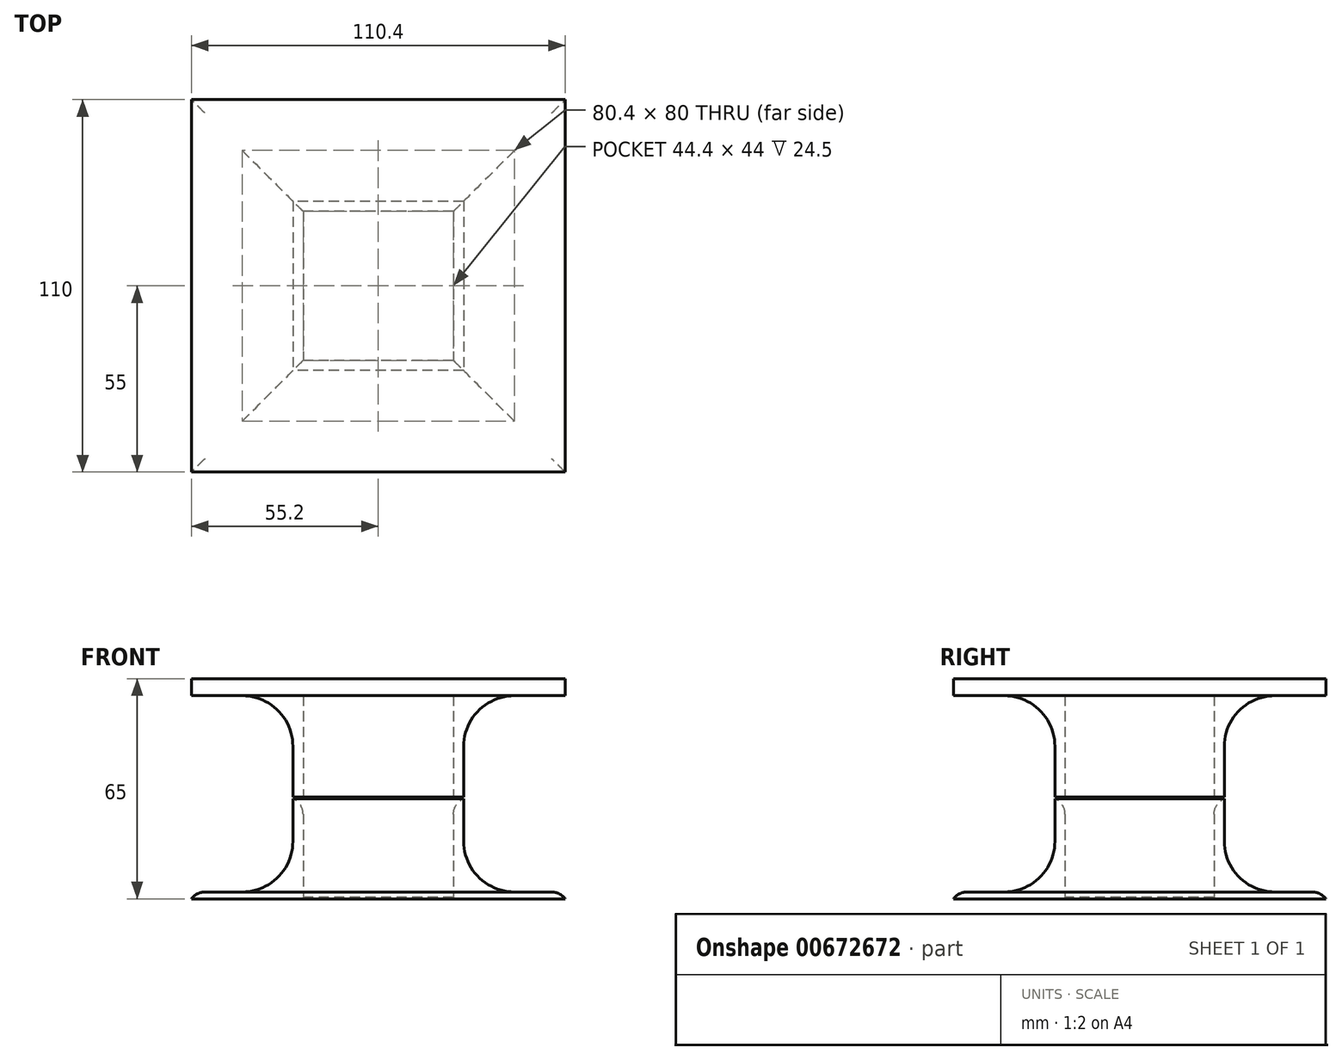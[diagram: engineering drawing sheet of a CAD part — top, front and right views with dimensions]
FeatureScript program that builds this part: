
annotation { "Feature Type Name" : "Feature", "Feature Type Description" : "" }
export const myFeature = defineFeature(function(context is Context, id is Id, definition is map)
    precondition{}
    {
        {
            var Q0;
            Q0=qCreatedBy(makeId("Top.planeOp"),FACE);
            var sketch = newSketch(context, id + "F0", { "sketchPlane" : qUnion([Q0])});
            skLineSegment(sketch, "E0.bottom", {"start": v(22.2, 22) * mm, "end": v(-22.2, 22) * mm});
            skLineSegment(sketch, "E0.top", {"start": v(22.2, -22) * mm, "end": v(-22.2, -22) * mm});
            skLineSegment(sketch, "E0.left", {"start": v(22.2, 22) * mm, "end": v(22.2, -22) * mm});
            skLineSegment(sketch, "E0.right", {"start": v(-22.2, 22) * mm, "end": v(-22.2, -22) * mm});
            skPoint(sketch, "E0.middle", {"position": v(0, 0) * mm});
            skLineSegment(sketch, "E1.bottom", {"start": v(55.2, 55) * mm, "end": v(-55.2, 55) * mm});
            skLineSegment(sketch, "E1.top", {"start": v(55.2, -55) * mm, "end": v(-55.2, -55) * mm});
            skLineSegment(sketch, "E1.left", {"start": v(55.2, 55) * mm, "end": v(55.2, -55) * mm});
            skLineSegment(sketch, "E1.right", {"start": v(-55.2, 55) * mm, "end": v(-55.2, -55) * mm});
            skLineSegment(sketch, "E2.0", {"start": v(25.2, 25) * mm, "end": v(25.2, -25) * mm});
            skLineSegment(sketch, "E2.1", {"start": v(25.2, 25) * mm, "end": v(-25.2, 25) * mm});
            skLineSegment(sketch, "E2.2", {"start": v(-25.2, 25) * mm, "end": v(-25.2, -25) * mm});
            skLineSegment(sketch, "E2.3", {"start": v(25.2, -25) * mm, "end": v(-25.2, -25) * mm});
            skLineSegment(sketch, "E3", {"start": v(25.2, 25) * mm, "end": v(25.2, 55) * mm, "construction": true});
            skLineSegment(sketch, "E4", {"start": v(25.2, 25) * mm, "end": v(55.2, 25) * mm, "construction": true});
            skSolve(sketch);
        }
        {
            var Q0;
            Q0=makeQuery(id+"F0.imprint","IMPRINT",FACE,{"disambiguationData":[TD([[makeQuery(id+"F0.imprint","IMPRINT",EDGE,{"derivedFrom":sQuery(id+"F0.wireOp",EDGE,"E1.bottom")}),1.0]])]});
            var Q1;
            Q1=makeQuery(id+"F0.imprint","IMPRINT",FACE,{"disambiguationData":[TD([[makeQuery(id+"F0.imprint","IMPRINT",EDGE,{"derivedFrom":sQuery(id+"F0.wireOp",EDGE,"E0.bottom")}),-1.0]])]});
            extrude(context, id + "F1", {"entities" : qUnion([Q0, Q1]), "depth" : 2 * mm, "offsetDistance" : 25 * mm});
        }
        {
            var Q0;
            Q0=makeQuery(id+"F0.imprint","IMPRINT",FACE,{"disambiguationData":[TD([[makeQuery(id+"F0.imprint","IMPRINT",EDGE,{"derivedFrom":sQuery(id+"F0.wireOp",EDGE,"E0.bottom")}),-1.0]])]});
            extrude(context, id + "F2", {"entities" : qUnion([Q0]), "operationType" : NewBodyOperationType.ADD, "depth" : 30 * mm, "offsetDistance" : 25 * mm});
        }
        {
            var Q0;
            Q0=makeQuery(id+"F2.opExtrude","CAP_FACE",FACE,{"disambiguationData":[OSD([sQuery(id+"F0.wireOp",EDGE,"E0.bottom"),sQuery(id+"F0.wireOp",EDGE,"E0.top"),sQuery(id+"F0.wireOp",EDGE,"E0.left"),sQuery(id+"F0.wireOp",EDGE,"E0.right"),sQuery(id+"F0.wireOp",EDGE,"E2.0"),sQuery(id+"F0.wireOp",EDGE,"E2.1"),sQuery(id+"F0.wireOp",EDGE,"E2.2"),sQuery(id+"F0.wireOp",EDGE,"E2.3")])],"isStart":false});
            extrude(context, id + "F3", {"entities" : qUnion([Q0]), "depth" : 30 * mm, "offsetDistance" : 25 * mm});
        }
        {
            var Q0;
            Q0=makeQuery(id+"F0.imprint","IMPRINT",FACE,{"disambiguationData":[TD([[makeQuery(id+"F0.imprint","IMPRINT",EDGE,{"derivedFrom":sQuery(id+"F0.wireOp",EDGE,"E0.bottom")}),1.0]])]});
            extrude(context, id + "F4", {"entities" : qUnion([Q0]), "operationType" : NewBodyOperationType.ADD, "depth" : 0.5 * mm, "offsetDistance" : 25 * mm});
        }
        {
            var Q0;
            Q0=makeQuery(id+"F0.imprint","IMPRINT",FACE,{"disambiguationData":[TD([[makeQuery(id+"F0.imprint","IMPRINT",EDGE,{"derivedFrom":sQuery(id+"F0.wireOp",EDGE,"E0.bottom")}),1.0]])]});
            var Q1;
            Q1=makeQuery(id+"F0.imprint","IMPRINT",FACE,{"disambiguationData":[TD([[makeQuery(id+"F0.imprint","IMPRINT",EDGE,{"derivedFrom":sQuery(id+"F0.wireOp",EDGE,"E0.bottom")}),-1.0]])]});
            var Q2;
            Q2=makeQuery(id+"F0.imprint","IMPRINT",FACE,{"disambiguationData":[TD([[makeQuery(id+"F0.imprint","IMPRINT",EDGE,{"derivedFrom":sQuery(id+"F0.wireOp",EDGE,"E1.bottom")}),1.0]])]});
            var Q3;
            Q3=makeQuery(id+"F3.opExtrude","CAP_FACE",FACE,{"disambiguationData":[OSD([sQuery(id+"F0.wireOp",EDGE,"E0.bottom"),sQuery(id+"F0.wireOp",EDGE,"E0.top"),sQuery(id+"F0.wireOp",EDGE,"E0.left"),sQuery(id+"F0.wireOp",EDGE,"E0.right"),sQuery(id+"F0.wireOp",EDGE,"E2.0"),sQuery(id+"F0.wireOp",EDGE,"E2.1"),sQuery(id+"F0.wireOp",EDGE,"E2.2"),sQuery(id+"F0.wireOp",EDGE,"E2.3")])],"isStart":false});
            extrude(context, id + "F5", {"entities" : qUnion([Q0, Q1, Q2]), "operationType" : NewBodyOperationType.ADD, "depth" : 65 * mm, "offsetDistance" : 25 * mm, "hasSecondDirection" : true, "secondDirectionBound" : SecondDirectionBoundingType.UP_TO_SURFACE, "secondDirectionOppositeDirection" : false, "secondDirectionDepth" : 35 * mm, "secondDirectionBoundEntityFace" : qUnion([Q3])});
        }
        {
            var Q0;
            Q0=makeQuery(id+"F2.boolean.opBoolean","INTERSECT",EDGE,{"derivedFrom":[makeQuery(id+"F1.opExtrude","CAP_FACE",FACE,{"disambiguationData":[OSD([sQuery(id+"F0.wireOp",EDGE,"E0.bottom"),sQuery(id+"F0.wireOp",EDGE,"E0.top"),sQuery(id+"F0.wireOp",EDGE,"E0.left"),sQuery(id+"F0.wireOp",EDGE,"E0.right"),sQuery(id+"F0.wireOp",EDGE,"E1.bottom"),sQuery(id+"F0.wireOp",EDGE,"E1.top"),sQuery(id+"F0.wireOp",EDGE,"E1.left"),sQuery(id+"F0.wireOp",EDGE,"E1.right")])],"isStart":false}),makeQuery(id+"F2.opExtrude","SWEPT_FACE",FACE,{"disambiguationData":[OSD([sQuery(id+"F0.wireOp",EDGE,"E2.0")])]})]});
            var Q1;
            Q1=makeQuery(id+"F2.boolean.opBoolean","INTERSECT",EDGE,{"derivedFrom":[makeQuery(id+"F1.opExtrude","CAP_FACE",FACE,{"disambiguationData":[OSD([sQuery(id+"F0.wireOp",EDGE,"E0.bottom"),sQuery(id+"F0.wireOp",EDGE,"E0.top"),sQuery(id+"F0.wireOp",EDGE,"E0.left"),sQuery(id+"F0.wireOp",EDGE,"E0.right"),sQuery(id+"F0.wireOp",EDGE,"E1.bottom"),sQuery(id+"F0.wireOp",EDGE,"E1.top"),sQuery(id+"F0.wireOp",EDGE,"E1.left"),sQuery(id+"F0.wireOp",EDGE,"E1.right")])],"isStart":false}),makeQuery(id+"F2.opExtrude","SWEPT_FACE",FACE,{"disambiguationData":[OSD([sQuery(id+"F0.wireOp",EDGE,"E2.3")])]})]});
            var Q2;
            Q2=makeQuery(id+"F2.boolean.opBoolean","INTERSECT",EDGE,{"derivedFrom":[makeQuery(id+"F1.opExtrude","CAP_FACE",FACE,{"disambiguationData":[OSD([sQuery(id+"F0.wireOp",EDGE,"E0.bottom"),sQuery(id+"F0.wireOp",EDGE,"E0.top"),sQuery(id+"F0.wireOp",EDGE,"E0.left"),sQuery(id+"F0.wireOp",EDGE,"E0.right"),sQuery(id+"F0.wireOp",EDGE,"E1.bottom"),sQuery(id+"F0.wireOp",EDGE,"E1.top"),sQuery(id+"F0.wireOp",EDGE,"E1.left"),sQuery(id+"F0.wireOp",EDGE,"E1.right")])],"isStart":false}),makeQuery(id+"F2.opExtrude","SWEPT_FACE",FACE,{"disambiguationData":[OSD([sQuery(id+"F0.wireOp",EDGE,"E2.2")])]})]});
            var Q3;
            Q3=makeQuery(id+"F2.boolean.opBoolean","INTERSECT",EDGE,{"derivedFrom":[makeQuery(id+"F1.opExtrude","CAP_FACE",FACE,{"disambiguationData":[OSD([sQuery(id+"F0.wireOp",EDGE,"E0.bottom"),sQuery(id+"F0.wireOp",EDGE,"E0.top"),sQuery(id+"F0.wireOp",EDGE,"E0.left"),sQuery(id+"F0.wireOp",EDGE,"E0.right"),sQuery(id+"F0.wireOp",EDGE,"E1.bottom"),sQuery(id+"F0.wireOp",EDGE,"E1.top"),sQuery(id+"F0.wireOp",EDGE,"E1.left"),sQuery(id+"F0.wireOp",EDGE,"E1.right")])],"isStart":false}),makeQuery(id+"F2.opExtrude","SWEPT_FACE",FACE,{"disambiguationData":[OSD([sQuery(id+"F0.wireOp",EDGE,"E2.1")])]})]});
            var Q4;
            Q4=makeQuery(id+"F3.opExtrude","CAP_EDGE",EDGE,{"disambiguationData":[OSD([sQuery(id+"F0.wireOp",EDGE,"E2.3")])],"isStart":false});
            var Q5;
            Q5=makeQuery(id+"F3.opExtrude","CAP_EDGE",EDGE,{"disambiguationData":[OSD([sQuery(id+"F0.wireOp",EDGE,"E2.2")])],"isStart":false});
            var Q6;
            Q6=makeQuery(id+"F3.opExtrude","CAP_EDGE",EDGE,{"disambiguationData":[OSD([sQuery(id+"F0.wireOp",EDGE,"E2.1")])],"isStart":false});
            var Q7;
            Q7=makeQuery(id+"F3.opExtrude","CAP_EDGE",EDGE,{"disambiguationData":[OSD([sQuery(id+"F0.wireOp",EDGE,"E2.0")])],"isStart":false});
            fillet(context, id + "F6", {"entities" : qUnion([Q0, Q1, Q2, Q3, Q4, Q5, Q6, Q7]), "radius" : 15 * mm, "tangentPropagation" : true, "allowEdgeOverflow" : false});
        }
        {
            var Q0;
            Q0=makeQuery(id+"F1.opExtrude","CAP_EDGE",EDGE,{"disambiguationData":[OSD([sQuery(id+"F0.wireOp",EDGE,"E1.bottom")])],"isStart":false});
            var Q1;
            Q1=makeQuery(id+"F1.opExtrude","CAP_EDGE",EDGE,{"disambiguationData":[OSD([sQuery(id+"F0.wireOp",EDGE,"E1.left")])],"isStart":false});
            var Q2;
            Q2=makeQuery(id+"F1.opExtrude","CAP_EDGE",EDGE,{"disambiguationData":[OSD([sQuery(id+"F0.wireOp",EDGE,"E1.right")])],"isStart":false});
            var Q3;
            Q3=makeQuery(id+"F1.opExtrude","CAP_EDGE",EDGE,{"disambiguationData":[OSD([sQuery(id+"F0.wireOp",EDGE,"E1.top")])],"isStart":false});
            fillet(context, id + "F7", {"entities" : qUnion([Q0, Q1, Q2, Q3]), "radius" : 5 * mm, "tangentPropagation" : true, "allowEdgeOverflow" : false});
        }
        {
            var Q0;
            Q0=makeQuery(id+"F2.opExtrude","CAP_EDGE",EDGE,{"disambiguationData":[OSD([sQuery(id+"F0.wireOp",EDGE,"E0.right")])],"isStart":false});
            var Q1;
            Q1=makeQuery(id+"F2.opExtrude","CAP_EDGE",EDGE,{"disambiguationData":[OSD([sQuery(id+"F0.wireOp",EDGE,"E0.top")])],"isStart":false});
            var Q2;
            Q2=makeQuery(id+"F2.opExtrude","CAP_EDGE",EDGE,{"disambiguationData":[OSD([sQuery(id+"F0.wireOp",EDGE,"E0.left")])],"isStart":false});
            var Q3;
            Q3=makeQuery(id+"F2.opExtrude","CAP_EDGE",EDGE,{"disambiguationData":[OSD([sQuery(id+"F0.wireOp",EDGE,"E0.bottom")])],"isStart":false});
            fillet(context, id + "F8", {"entities" : qUnion([Q0, Q1, Q2, Q3]), "radius" : 5 * mm, "tangentPropagation" : true, "allowEdgeOverflow" : false});
        }
    });
